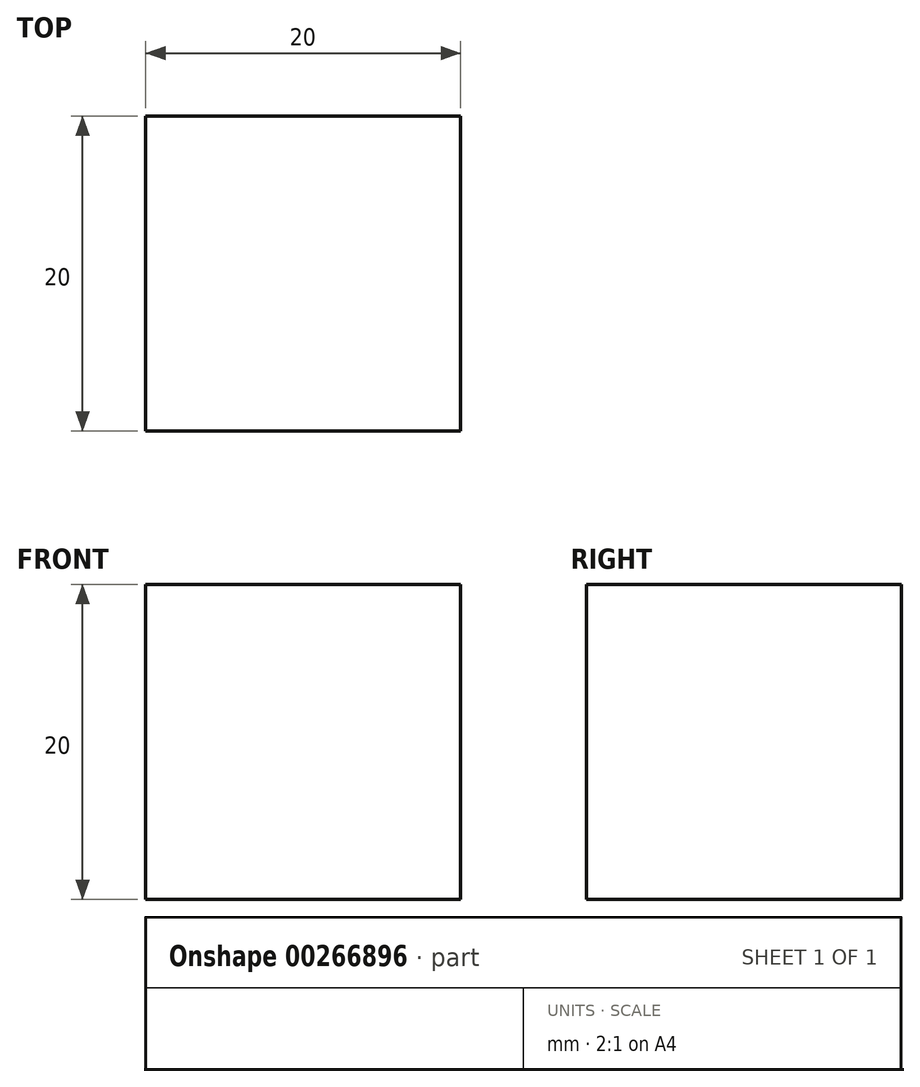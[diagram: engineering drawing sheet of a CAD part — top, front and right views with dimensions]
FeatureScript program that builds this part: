
annotation { "Feature Type Name" : "Feature", "Feature Type Description" : "" }
export const myFeature = defineFeature(function(context is Context, id is Id, definition is map)
    precondition{}
    {
        {
            var Q0;
            Q0=qCreatedBy(makeId("Top.planeOp"),FACE);
            var sketch = newSketch(context, id + "F0", { "sketchPlane" : qUnion([Q0])});
            skLineSegment(sketch, "E0.bottom", {"start": v(10, 10) * mm, "end": v(-10, 10) * mm});
            skLineSegment(sketch, "E0.top", {"start": v(10, -10) * mm, "end": v(-10, -10) * mm});
            skLineSegment(sketch, "E0.left", {"start": v(10, 10) * mm, "end": v(10, -10) * mm});
            skLineSegment(sketch, "E0.right", {"start": v(-10, 10) * mm, "end": v(-10, -10) * mm});
            skPoint(sketch, "E0.middle", {"position": v(0, 0) * mm});
            skSolve(sketch);
        }
        {
            var Q0;
            Q0 = qSketchRegion(id + "F0", true);
            extrude(context, id + "F1", {"entities" : qUnion([Q0]), "depth" : 20 * mm});
        }
    });
